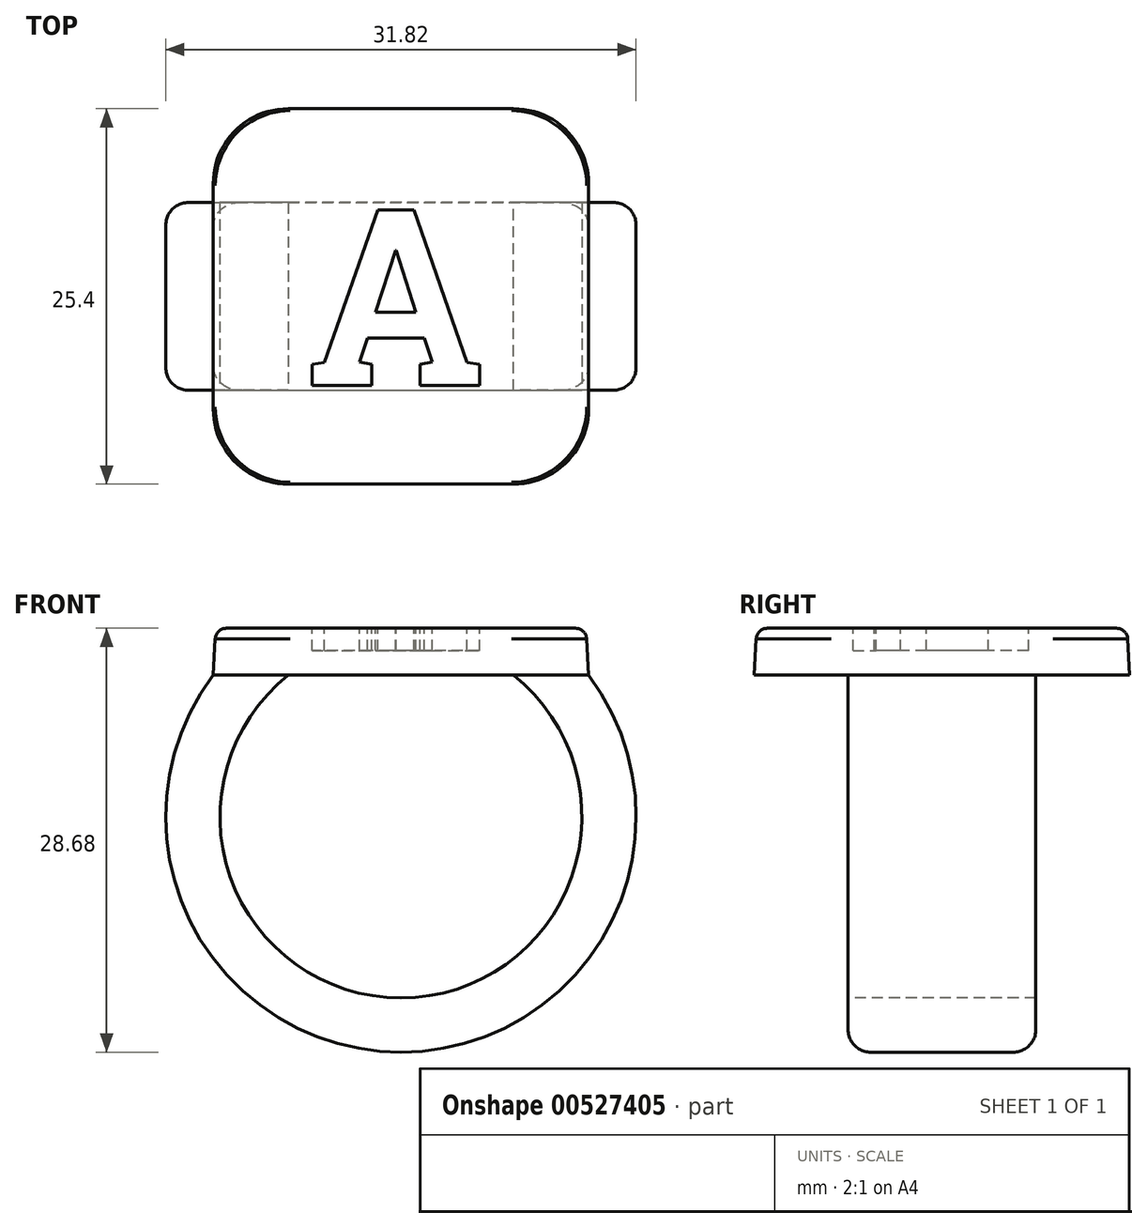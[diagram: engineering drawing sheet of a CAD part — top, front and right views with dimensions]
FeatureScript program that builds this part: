
annotation { "Feature Type Name" : "Feature", "Feature Type Description" : "" }
export const myFeature = defineFeature(function(context is Context, id is Id, definition is map)
    precondition{}
    {
        {
            var Q0;
            Q0=qCreatedBy(makeId("Top.planeOp"),FACE);
            var sketch = newSketch(context, id + "F0", { "sketchPlane" : qUnion([Q0])});
            skLineSegment(sketch, "E0.bottom", {"start": v(12.7, -12.7) * mm, "end": v(-12.7, -12.7) * mm});
            skLineSegment(sketch, "E0.top", {"start": v(12.7, 12.7) * mm, "end": v(-12.7, 12.7) * mm});
            skLineSegment(sketch, "E0.left", {"start": v(12.7, -12.7) * mm, "end": v(12.7, 12.7) * mm});
            skLineSegment(sketch, "E0.right", {"start": v(-12.7, -12.7) * mm, "end": v(-12.7, 12.7) * mm});
            skPoint(sketch, "E0.middle", {"position": v(0, 0) * mm});
            skSolve(sketch);
        }
        {
            var Q0;
            Q0 = qSketchRegion(id + "F0", true);
            extrude(context, id + "F1", {"entities" : qUnion([Q0]), "depth" : 3.17 * mm, "offsetDistance" : 25.4 * mm, "hasDraft" : true, "draftAngle" : 3 * degree, "draftPullDirection" : true});
        }
        {
            var Q0;
            Q0=makeQuery(id+"F1.opExtrude","CAP_FACE",FACE,{"disambiguationData":[OSD([sQuery(id+"F0.wireOp",EDGE,"E0.bottom"),sQuery(id+"F0.wireOp",EDGE,"E0.top"),sQuery(id+"F0.wireOp",EDGE,"E0.left"),sQuery(id+"F0.wireOp",EDGE,"E0.right")])],"isStart":true});
            var sketch = newSketch(context, id + "F2", { "sketchPlane" : qUnion([Q0])});
            skSolve(sketch);
        }
        {
            var Q0;
            Q0=qCreatedBy(makeId("Front.planeOp"),FACE);
            var sketch = newSketch(context, id + "F3", { "sketchPlane" : qUnion([Q0])});
            skArc(sketch, "E1", {"start": v(-10.16, 0) * mm, "mid": v(0, -23.56) * mm, "end": v(10.16, 0) * mm});
            skSolve(sketch);
        }
        {
            var Q0;
            Q0=makeQuery(id+"F2.imprint","IMPRINT",FACE,{"disambiguationData":[TD([[makeQuery(id+"F2.imprint","IMPRINT",EDGE,{"derivedFrom":makeQuery(id+"F1.opExtrude","CAP_EDGE",EDGE,{"disambiguationData":[OSD([sQuery(id+"F0.wireOp",EDGE,"E0.bottom")])],"isStart":true})}),1.0]])]});
            var sketch = newSketch(context, id + "F4", { "sketchPlane" : qUnion([Q0])});
            skLineSegment(sketch, "E2.bottom", {"start": v(-7.62, -6.35) * mm, "end": v(-12.7, -6.35) * mm});
            skLineSegment(sketch, "E2.top", {"start": v(-7.62, 6.35) * mm, "end": v(-12.7, 6.35) * mm});
            skLineSegment(sketch, "E2.left", {"start": v(-7.62, -6.35) * mm, "end": v(-7.62, 6.35) * mm});
            skLineSegment(sketch, "E2.right", {"start": v(-12.7, -6.35) * mm, "end": v(-12.7, 6.35) * mm});
            skPoint(sketch, "E2.middle", {"position": v(-10.16, 0) * mm});
            skSolve(sketch);
        }
        {
            var Q0;
            Q0 = qSketchRegion(id + "F4", true);
            var Q1;
            Q1 = qConstructionFilter(qBodyType(qCreatedBy(id + "F3" ,EDGE), BodyType.WIRE), ConstructionObject.NO);
            sweep(context, id + "F5", {"operationType" : NewBodyOperationType.ADD, "profiles" : qUnion([Q0]), "path" : qUnion([Q1])});
        }
        {
            var Q0;
            Q0=qCreatedBy(makeId("Front.planeOp"),FACE);
            var sketch = newSketch(context, id + "F6", { "sketchPlane" : qUnion([Q0])});
            skLineSegment(sketch, "E3.3", {"start": v(10.16, 0) * mm, "end": v(7.62, 0) * mm});
            skLineSegment(sketch, "E3.4", {"start": v(10.01, -2.54) * mm, "end": v(10.16, 0) * mm});
            skArc(sketch, "E3.5", {"start": v(10.01, -2.54) * mm, "mid": v(8.9, -1.18) * mm, "end": v(7.62, 0) * mm});
            skSolve(sketch);
        }
        {
            var Q0;
            Q0 = qSketchRegion(id + "F6", true);
            var Q1;
            Q1=makeQuery(id+"F5.opSweep","SWEPT_FACE",FACE,{"disambiguationData":[OSD([sQuery(id+"F3.wireOp",EDGE,"E1"),sQuery(id+"F4.wireOp",EDGE,"E2.top")])]});
            var Q2;
            Q2=makeQuery(id+"F5.opSweep","SWEPT_FACE",FACE,{"disambiguationData":[OSD([sQuery(id+"F3.wireOp",EDGE,"E1"),sQuery(id+"F4.wireOp",EDGE,"E2.bottom")])]});
            extrude(context, id + "F7", {"entities" : qUnion([Q0]), "operationType" : NewBodyOperationType.ADD, "endBound" : BoundingType.UP_TO_SURFACE, "depth" : 25.4 * mm, "endBoundEntityFace" : qUnion([Q1]), "offsetDistance" : 25.4 * mm, "hasSecondDirection" : true, "secondDirectionBound" : SecondDirectionBoundingType.UP_TO_SURFACE, "secondDirectionOppositeDirection" : true, "secondDirectionDepth" : 25.4 * mm, "secondDirectionBoundEntityFace" : qUnion([Q2])});
        }
        {
            var Q0;
            Q0=makeQuery(id+"F1.opExtrude","SWEPT_EDGE",EDGE,{"disambiguationData":[OSD([sQuery(id+"F0.wireOp",EDGE,"E0.bottom"),sQuery(id+"F0.wireOp",EDGE,"E0.left")])]});
            var Q1;
            Q1=makeQuery(id+"F1.opExtrude","SWEPT_EDGE",EDGE,{"disambiguationData":[OSD([sQuery(id+"F0.wireOp",EDGE,"E0.bottom"),sQuery(id+"F0.wireOp",EDGE,"E0.right")])]});
            var Q2;
            Q2=makeQuery(id+"F1.opExtrude","SWEPT_EDGE",EDGE,{"disambiguationData":[OSD([sQuery(id+"F0.wireOp",EDGE,"E0.top"),sQuery(id+"F0.wireOp",EDGE,"E0.right")])]});
            var Q3;
            Q3=makeQuery(id+"F1.opExtrude","SWEPT_EDGE",EDGE,{"disambiguationData":[OSD([sQuery(id+"F0.wireOp",EDGE,"E0.top"),sQuery(id+"F0.wireOp",EDGE,"E0.left")])]});
            fillet(context, id + "F8", {"entities" : qUnion([Q0, Q1, Q2, Q3]), "radius" : 5.08 * mm, "tangentPropagation" : true, "allowEdgeOverflow" : false});
        }
        {
            var Q0;
            Q0=makeQuery(id+"F5.opSweep","SWEPT_EDGE",EDGE,{"disambiguationData":[OSD([sQuery(id+"F0.wireOp",EDGE,"E0.right"),sQuery(id+"F3.wireOp",EDGE,"E1"),sQuery(id+"F4.wireOp",EDGE,"E2.top"),sQuery(id+"F4.wireOp",EDGE,"E2.right")])]});
            var Q1;
            Q1=makeQuery(id+"F5.opSweep","SWEPT_EDGE",EDGE,{"disambiguationData":[OSD([sQuery(id+"F0.wireOp",EDGE,"E0.right"),sQuery(id+"F3.wireOp",EDGE,"E1"),sQuery(id+"F4.wireOp",EDGE,"E2.bottom"),sQuery(id+"F4.wireOp",EDGE,"E2.right")])]});
            fillet(context, id + "F9", {"entities" : qUnion([Q0, Q1]), "radius" : 1.52 * mm, "tangentPropagation" : true, "allowEdgeOverflow" : false});
        }
        {
            var Q0;
            Q0=makeQuery(id+"F1.opExtrude","CAP_EDGE",EDGE,{"disambiguationData":[OSD([sQuery(id+"F0.wireOp",EDGE,"E0.bottom")])],"isStart":false});
            var Q1;
            Q1=makeQuery(id+"F1.opExtrude","CAP_EDGE",EDGE,{"disambiguationData":[OSD([sQuery(id+"F0.wireOp",EDGE,"E0.left")])],"isStart":false});
            var Q2;
            Q2=makeQuery(id+"F1.opExtrude","CAP_EDGE",EDGE,{"disambiguationData":[OSD([sQuery(id+"F0.wireOp",EDGE,"E0.top")])],"isStart":false});
            var Q3;
            Q3=makeQuery(id+"F1.opExtrude","CAP_EDGE",EDGE,{"disambiguationData":[OSD([sQuery(id+"F0.wireOp",EDGE,"E0.right")])],"isStart":false});
            var Q4;
            {var subQ0=sQuery(id+"F0.wireOp",EDGE,"E0.right");var subQ1=sQuery(id+"F0.wireOp",EDGE,"E0.bottom");Q4=makeQuery(id+"F8.opFillet","BLEND_EDGE",EDGE,{"blendedFrom":[makeQuery(id+"F1.opExtrude","SWEPT_EDGE",EDGE,{"disambiguationData":[OSD([subQ1,subQ0])]}),makeQuery(id+"F1.opExtrude","CAP_FACE",FACE,{"disambiguationData":[OSD([subQ1,sQuery(id+"F0.wireOp",EDGE,"E0.top"),sQuery(id+"F0.wireOp",EDGE,"E0.left"),subQ0])],"isStart":false})],"blendedInto":[makeQuery(id+"F1.opExtrude","CAP_FACE",FACE,{"disambiguationData":[OSD([subQ1,sQuery(id+"F0.wireOp",EDGE,"E0.top"),sQuery(id+"F0.wireOp",EDGE,"E0.left"),subQ0])],"isStart":false})]});}
            var Q5;
            {var subQ0=sQuery(id+"F0.wireOp",EDGE,"E0.left");var subQ1=sQuery(id+"F0.wireOp",EDGE,"E0.bottom");Q5=makeQuery(id+"F8.opFillet","BLEND_EDGE",EDGE,{"blendedFrom":[makeQuery(id+"F1.opExtrude","SWEPT_EDGE",EDGE,{"disambiguationData":[OSD([subQ1,subQ0])]}),makeQuery(id+"F1.opExtrude","CAP_FACE",FACE,{"disambiguationData":[OSD([subQ1,sQuery(id+"F0.wireOp",EDGE,"E0.top"),subQ0,sQuery(id+"F0.wireOp",EDGE,"E0.right")])],"isStart":false})],"blendedInto":[makeQuery(id+"F1.opExtrude","CAP_FACE",FACE,{"disambiguationData":[OSD([subQ1,sQuery(id+"F0.wireOp",EDGE,"E0.top"),subQ0,sQuery(id+"F0.wireOp",EDGE,"E0.right")])],"isStart":false})]});}
            var Q6;
            {var subQ0=sQuery(id+"F0.wireOp",EDGE,"E0.left");var subQ1=sQuery(id+"F0.wireOp",EDGE,"E0.top");Q6=makeQuery(id+"F8.opFillet","BLEND_EDGE",EDGE,{"blendedFrom":[makeQuery(id+"F1.opExtrude","SWEPT_EDGE",EDGE,{"disambiguationData":[OSD([subQ1,subQ0])]}),makeQuery(id+"F1.opExtrude","CAP_FACE",FACE,{"disambiguationData":[OSD([sQuery(id+"F0.wireOp",EDGE,"E0.bottom"),subQ1,subQ0,sQuery(id+"F0.wireOp",EDGE,"E0.right")])],"isStart":false})],"blendedInto":[makeQuery(id+"F1.opExtrude","CAP_FACE",FACE,{"disambiguationData":[OSD([sQuery(id+"F0.wireOp",EDGE,"E0.bottom"),subQ1,subQ0,sQuery(id+"F0.wireOp",EDGE,"E0.right")])],"isStart":false})]});}
            var Q7;
            {var subQ0=sQuery(id+"F0.wireOp",EDGE,"E0.right");var subQ1=sQuery(id+"F0.wireOp",EDGE,"E0.top");Q7=makeQuery(id+"F8.opFillet","BLEND_EDGE",EDGE,{"blendedFrom":[makeQuery(id+"F1.opExtrude","SWEPT_EDGE",EDGE,{"disambiguationData":[OSD([subQ1,subQ0])]}),makeQuery(id+"F1.opExtrude","CAP_FACE",FACE,{"disambiguationData":[OSD([sQuery(id+"F0.wireOp",EDGE,"E0.bottom"),subQ1,sQuery(id+"F0.wireOp",EDGE,"E0.left"),subQ0])],"isStart":false})],"blendedInto":[makeQuery(id+"F1.opExtrude","CAP_FACE",FACE,{"disambiguationData":[OSD([sQuery(id+"F0.wireOp",EDGE,"E0.bottom"),subQ1,sQuery(id+"F0.wireOp",EDGE,"E0.left"),subQ0])],"isStart":false})]});}
            fillet(context, id + "F10", {"entities" : qUnion([Q0, Q1, Q2, Q3, Q4, Q5, Q6, Q7]), "radius" : 0.76 * mm, "tangentPropagation" : true, "allowEdgeOverflow" : false});
        }
        {
            var Q0;
            Q0=makeQuery(id+"F1.opExtrude","CAP_FACE",FACE,{"disambiguationData":[OSD([sQuery(id+"F0.wireOp",EDGE,"E0.bottom"),sQuery(id+"F0.wireOp",EDGE,"E0.top"),sQuery(id+"F0.wireOp",EDGE,"E0.left"),sQuery(id+"F0.wireOp",EDGE,"E0.right")])],"isStart":false});
            var sketch = newSketch(context, id + "F11", { "sketchPlane" : qUnion([Q0])});
            skText(sketch, "E4", { "text": "A", "fontName": "RobotoSlab-Bold.ttf"});
            const initialGuessF11  = {"E4": [-0.00635, -0.00602, 1, 0, 0.01203]};
            skSetInitialGuess(sketch, initialGuessF11);
            skSolve(sketch);
        }
        {
            var Q0;
            Q0 = qSketchRegion(id + "F11", true);
            extrude(context, id + "F12", {"entities" : qUnion([Q0]), "operationType" : NewBodyOperationType.REMOVE, "oppositeDirection" : true, "depth" : 1.52 * mm, "offsetDistance" : 25.4 * mm});
        }
    });
